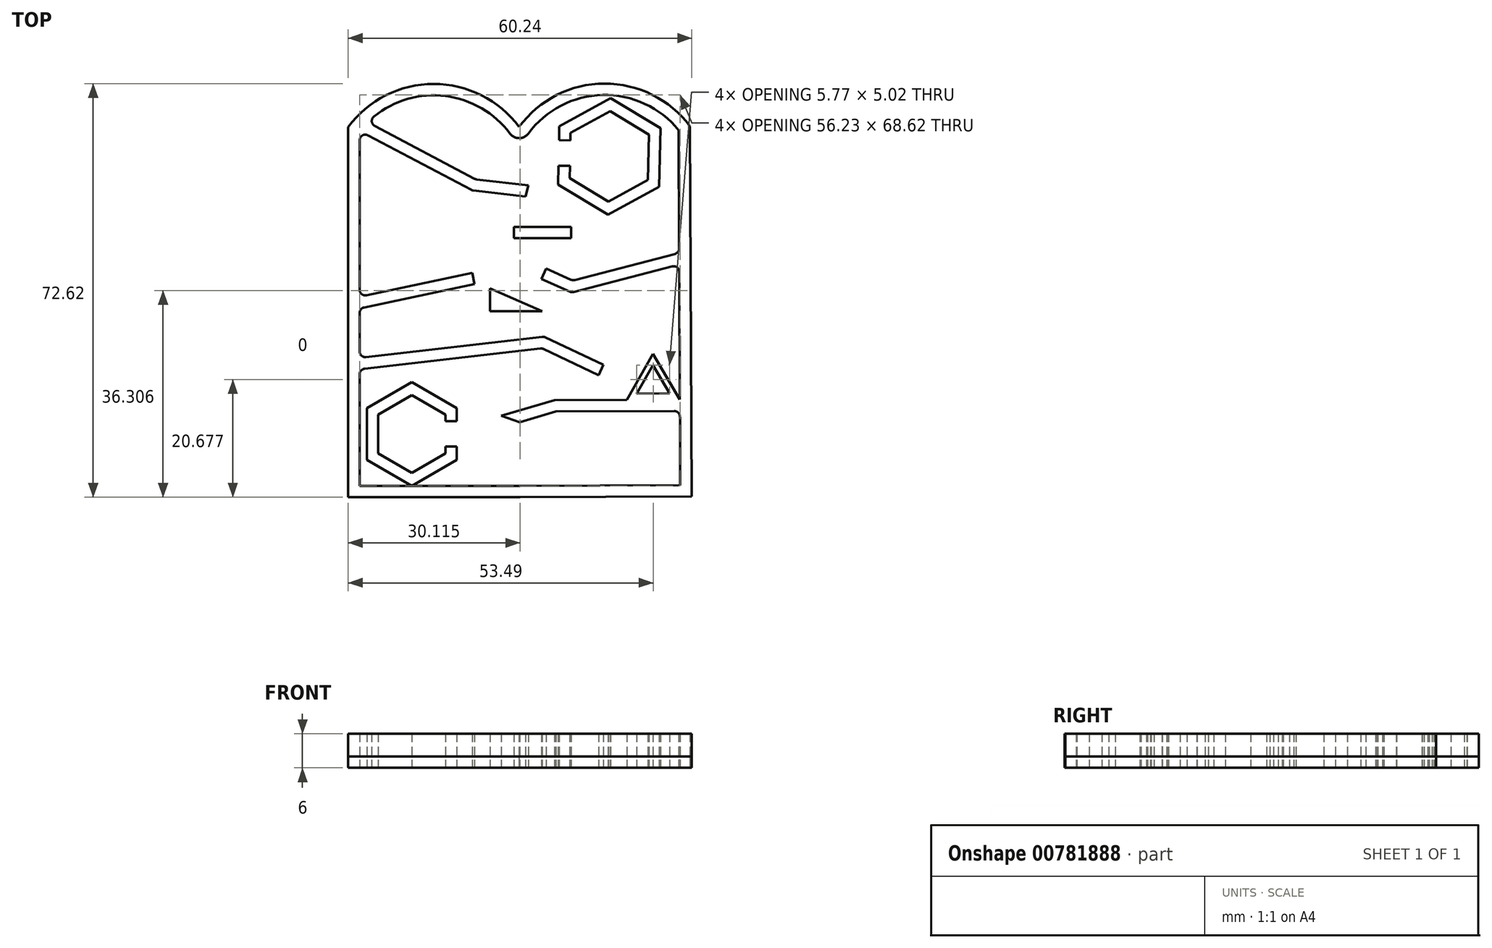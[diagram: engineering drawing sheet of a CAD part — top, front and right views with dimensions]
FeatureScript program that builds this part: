
annotation { "Feature Type Name" : "Feature", "Feature Type Description" : "" }
export const myFeature = defineFeature(function(context is Context, id is Id, definition is map)
    precondition{}
    {
        {
            var Q0;
            Q0=qCreatedBy(makeId("Top.planeOp"),FACE);
            var sketch = newSketch(context, id + "F0", { "sketchPlane" : qUnion([Q0])});
            skCircle(sketch, "E0", {"center": v(0, 0) * mm, "radius": 50 * mm, "construction": true});
            skLineSegment(sketch, "E1.top", {"start": v(-30, -32.65) * mm, "end": v(0.32, -32.65) * mm});
            skLineSegment(sketch, "E1.left", {"start": v(-30, 32.35) * mm, "end": v(-30, -32.65) * mm});
            skArc(sketch, "E2", {"start": v(-0.02, 32.38) * mm, "mid": v(-15.02, 39.9) * mm, "end": v(-30, 32.35) * mm});
            skLineSegment(sketch, "E3", {"start": v(0, 21.27) * mm, "end": v(0, 21.27) * mm});
            skLineSegment(sketch, "E4.0", {"start": v(-28, -30.65) * mm, "end": v(0.11, -30.65) * mm});
            skLineSegment(sketch, "E4.1", {"start": v(-28, 30) * mm, "end": v(-28, 3.79) * mm});
            skArc(sketch, "E4.2", {"start": v(-1.64, 31.2) * mm, "mid": v(-12.94, 37.77) * mm, "end": v(-25.5, 34.18) * mm});
            skArc(sketch, "E5.MirrorCS", {"start": v(-0.02, 32.38) * mm, "mid": v(14.94, 39.97) * mm, "end": v(29.95, 32.48) * mm});
            skArc(sketch, "E6.MirrorCS", {"start": v(1.6, 31.21) * mm, "mid": v(14.64, 37.96) * mm, "end": v(27.95, 31.8) * mm});
            skLineSegment(sketch, "E7.MirrorCS", {"start": v(27.95, 31.8) * mm, "end": v(28.05, 11.04) * mm});
            skLineSegment(sketch, "E8.MirrorCS", {"start": v(29.95, 32.48) * mm, "end": v(30.24, -32.52) * mm});
            skLineSegment(sketch, "E9.MirrorCS", {"start": v(28.23, -30.53) * mm, "end": v(0.11, -30.65) * mm});
            skLineSegment(sketch, "E10.MirrorCS", {"start": v(30.24, -32.52) * mm, "end": v(-0.08, -32.65) * mm});
            skLineSegment(sketch, "E11", {"start": v(-26.53, 30.89) * mm, "end": v(-8.45, 21.32) * mm});
            skLineSegment(sketch, "E12", {"start": v(-8.1, 21.21) * mm, "end": v(1.11, 20.14) * mm});
            skLineSegment(sketch, "E13", {"start": v(26.81, 7.87) * mm, "end": v(9.54, 3.39) * mm});
            skLineSegment(sketch, "E14", {"start": v(8.88, 3.44) * mm, "end": v(3.9, 5.68) * mm});
            skLineSegment(sketch, "E15", {"start": v(-27.2, 0.68) * mm, "end": v(-7.88, 4.78) * mm});
            skLineSegment(sketch, "E16", {"start": v(-27.11, -10.08) * mm, "end": v(3.67, -6.53) * mm});
            skLineSegment(sketch, "E17", {"start": v(4.21, -6.62) * mm, "end": v(13.89, -11.2) * mm});
            skLineSegment(sketch, "E18", {"start": v(27.17, -17.5) * mm, "end": v(6.43, -17.6) * mm});
            skLineSegment(sketch, "E19", {"start": v(6.43, -17.6) * mm, "end": v(0.1, -19.46) * mm});
            skLineSegment(sketch, "E20.0", {"start": v(-7.5, 23.16) * mm, "end": v(1.59, 22.1) * mm});
            skLineSegment(sketch, "E20.1", {"start": v(-25.34, 32.52) * mm, "end": v(-7.84, 23.26) * mm});
            skLineSegment(sketch, "E21", {"start": v(1.59, 22.1) * mm, "end": v(1.11, 20.14) * mm});
            skLineSegment(sketch, "E22.0", {"start": v(9.06, 5.56) * mm, "end": v(4.72, 7.5) * mm});
            skLineSegment(sketch, "E22.1", {"start": v(27.3, 10.07) * mm, "end": v(9.72, 5.5) * mm});
            skLineSegment(sketch, "E23", {"start": v(4.72, 7.5) * mm, "end": v(3.9, 5.68) * mm});
            skLineSegment(sketch, "E24.0", {"start": v(-26.8, 2.8) * mm, "end": v(-8.23, 6.75) * mm});
            skLineSegment(sketch, "E25.0", {"start": v(4.55, -4.57) * mm, "end": v(14.74, -9.4) * mm});
            skLineSegment(sketch, "E25.1", {"start": v(-26.89, -8.04) * mm, "end": v(4, -4.48) * mm});
            skLineSegment(sketch, "E26", {"start": v(14.74, -9.4) * mm, "end": v(13.89, -11.2) * mm});
            skLineSegment(sketch, "E27.0", {"start": v(6.14, -15.6) * mm, "end": v(-3.14, -18.32) * mm});
            skLineSegment(sketch, "E28", {"start": v(0.1, -19.46) * mm, "end": v(-3.14, -18.32) * mm});
            skLineSegment(sketch, "E29", {"start": v(-8.23, 6.75) * mm, "end": v(-7.88, 4.78) * mm});
            skCircle(sketch, "E30.cCircle", {"center": v(15.78, 27.19) * mm, "radius": 7.93 * mm, "construction": true});
            skLineSegment(sketch, "E30.0", {"start": v(22.56, 23.08) * mm, "end": v(15.62, 19.26) * mm});
            skLineSegment(sketch, "E30.1", {"start": v(15.62, 19.26) * mm, "end": v(8.83, 23.36) * mm});
            skLineSegment(sketch, "E30.2", {"start": v(8.83, 23.36) * mm, "end": v(8.88, 25.5) * mm});
            skLineSegment(sketch, "E30.3", {"start": v(9, 31.3) * mm, "end": v(15.94, 35.11) * mm});
            skLineSegment(sketch, "E30.4", {"start": v(15.94, 35.11) * mm, "end": v(22.73, 31) * mm});
            skLineSegment(sketch, "E30.5", {"start": v(22.73, 31) * mm, "end": v(22.56, 23.08) * mm});
            skLineSegment(sketch, "E31", {"start": v(8.97, 30) * mm, "end": v(9, 31.3) * mm});
            skLineSegment(sketch, "E32.0", {"start": v(6.8, 22.25) * mm, "end": v(6.88, 25.55) * mm});
            skLineSegment(sketch, "E32.1", {"start": v(15.57, 16.95) * mm, "end": v(6.8, 22.25) * mm});
            skLineSegment(sketch, "E32.2", {"start": v(24.54, 21.88) * mm, "end": v(15.57, 16.95) * mm});
            skLineSegment(sketch, "E32.3", {"start": v(6.97, 30.05) * mm, "end": v(7.02, 32.49) * mm});
            skLineSegment(sketch, "E32.4", {"start": v(7.02, 32.49) * mm, "end": v(16, 37.42) * mm});
            skLineSegment(sketch, "E32.5", {"start": v(16, 37.42) * mm, "end": v(24.75, 32.12) * mm});
            skLineSegment(sketch, "E32.6", {"start": v(24.75, 32.12) * mm, "end": v(24.54, 21.88) * mm});
            skLineSegment(sketch, "E33", {"start": v(6.88, 25.55) * mm, "end": v(8.88, 25.5) * mm});
            skLineSegment(sketch, "E34", {"start": v(8.97, 30) * mm, "end": v(6.97, 30.05) * mm});
            skLineSegment(sketch, "E35", {"start": v(28.06, 6.91) * mm, "end": v(28.16, -15.5) * mm});
            skLineSegment(sketch, "E36", {"start": v(-28, 31.67) * mm, "end": v(-28, 31.67) * mm});
            skLineSegment(sketch, "E37", {"start": v(-28, -0.3) * mm, "end": v(-28, -7.04) * mm});
            skLineSegment(sketch, "E38", {"start": v(-28, -11.07) * mm, "end": v(-28, -30.65) * mm});
            skLineSegment(sketch, "E39", {"start": v(28.18, -18.5) * mm, "end": v(28.23, -30.53) * mm});
            skLineSegment(sketch, "E40", {"start": v(-0.93, 14.82) * mm, "end": v(-0.93, 12.82) * mm});
            skLineSegment(sketch, "E41", {"start": v(-0.93, 12.82) * mm, "end": v(9.07, 12.82) * mm});
            skLineSegment(sketch, "E42", {"start": v(9.07, 12.82) * mm, "end": v(9.07, 14.82) * mm});
            skLineSegment(sketch, "E43", {"start": v(9.07, 14.82) * mm, "end": v(-0.93, 14.82) * mm});
            skCircle(sketch, "E44.cCircle", {"center": v(23.48, -12.8) * mm, "radius": 3.33 * mm, "construction": true});
            skLineSegment(sketch, "E44.0", {"start": v(23.45, -9.46) * mm, "end": v(26.37, -14.43) * mm});
            skLineSegment(sketch, "E44.1", {"start": v(26.37, -14.43) * mm, "end": v(20.6, -14.48) * mm});
            skLineSegment(sketch, "E44.2", {"start": v(20.6, -14.48) * mm, "end": v(23.45, -9.46) * mm});
            skCircle(sketch, "E45.cCircle", {"center": v(-18.86, -21.54) * mm, "radius": 6.8 * mm, "construction": true});
            skLineSegment(sketch, "E45.0", {"start": v(-18.86, -14.74) * mm, "end": v(-12.97, -18.14) * mm});
            skLineSegment(sketch, "E45.1", {"start": v(-12.97, -18.14) * mm, "end": v(-12.97, -19.27) * mm});
            skLineSegment(sketch, "E45.2", {"start": v(-12.97, -24.94) * mm, "end": v(-18.86, -28.34) * mm});
            skLineSegment(sketch, "E45.3", {"start": v(-18.86, -28.34) * mm, "end": v(-24.75, -24.94) * mm});
            skLineSegment(sketch, "E45.4", {"start": v(-24.75, -24.94) * mm, "end": v(-24.75, -18.14) * mm});
            skLineSegment(sketch, "E45.5", {"start": v(-24.75, -18.14) * mm, "end": v(-18.86, -14.74) * mm});
            skLineSegment(sketch, "E46.2", {"start": v(23.43, -7.46) * mm, "end": v(28.16, -15.5) * mm});
            skLineSegment(sketch, "E47", {"start": v(18.85, -15.55) * mm, "end": v(18.85, -15.55) * mm});
            skLineSegment(sketch, "E48", {"start": v(28.16, -15.5) * mm, "end": v(28.16, -15.5) * mm});
            skLineSegment(sketch, "E49", {"start": v(18.85, -15.55) * mm, "end": v(23.43, -7.46) * mm});
            skLineSegment(sketch, "E50", {"start": v(18.85, -15.55) * mm, "end": v(6.14, -15.6) * mm});
            skLineSegment(sketch, "E51", {"start": v(-12.97, -23.77) * mm, "end": v(-12.97, -24.94) * mm});
            skLineSegment(sketch, "E52.0", {"start": v(-10.97, -16.99) * mm, "end": v(-10.97, -19.27) * mm});
            skLineSegment(sketch, "E52.1", {"start": v(-18.86, -12.44) * mm, "end": v(-10.97, -16.99) * mm});
            skLineSegment(sketch, "E52.2", {"start": v(-26.75, -16.99) * mm, "end": v(-18.86, -12.44) * mm});
            skLineSegment(sketch, "E52.3", {"start": v(-10.97, -23.77) * mm, "end": v(-10.97, -26.1) * mm});
            skLineSegment(sketch, "E52.4", {"start": v(-10.97, -26.1) * mm, "end": v(-18.86, -30.65) * mm});
            skLineSegment(sketch, "E52.5", {"start": v(-18.86, -30.65) * mm, "end": v(-26.75, -26.1) * mm});
            skLineSegment(sketch, "E52.6", {"start": v(-26.75, -26.1) * mm, "end": v(-26.75, -16.99) * mm});
            skLineSegment(sketch, "E53", {"start": v(-12.97, -23.77) * mm, "end": v(-10.97, -23.77) * mm});
            skLineSegment(sketch, "E54", {"start": v(-12.97, -19.27) * mm, "end": v(-10.97, -19.27) * mm});
            skLineSegment(sketch, "E55", {"start": v(-5.14, 0) * mm, "end": v(-5.14, 4) * mm});
            skLineSegment(sketch, "E56", {"start": v(-5.14, 4) * mm, "end": v(4.03, 0) * mm});
            skLineSegment(sketch, "E57", {"start": v(4.03, 0) * mm, "end": v(-5.14, 0) * mm});
            skPoint(sketch, "E58.visualSharp", {"position": v(-26.61, 33.2) * mm});
            skArc(sketch, "E58.filletArc", {"start": v(-25.5, 34.18) * mm, "mid": v(-25.86, 33.3) * mm, "end": v(-25.34, 32.52) * mm});
            skPoint(sketch, "E59.orphan", {"position": v(-0.05, 32.35) * mm});
            skPoint(sketch, "E60.start.orphan", {"position": v(0, 32.35) * mm});
            skArc(sketch, "E61", {"start": v(-1.64, 31.2) * mm, "mid": v(-0.02, 30.4) * mm, "end": v(1.6, 31.21) * mm});
            skPoint(sketch, "E62.visualSharp", {"position": v(-28, 31.67) * mm});
            skArc(sketch, "E62.filletArc", {"start": v(-26.53, 30.89) * mm, "mid": v(-27.52, 30.86) * mm, "end": v(-28, 30) * mm});
            skPoint(sketch, "E63.visualSharp", {"position": v(28.05, 10.26) * mm});
            skArc(sketch, "E63.filletArc", {"start": v(27.3, 10.07) * mm, "mid": v(27.84, 10.42) * mm, "end": v(28.05, 11.04) * mm});
            skPoint(sketch, "E64.visualSharp", {"position": v(28.06, 8.2) * mm});
            skArc(sketch, "E64.filletArc", {"start": v(28.06, 6.91) * mm, "mid": v(27.67, 7.7) * mm, "end": v(26.81, 7.87) * mm});
            skPoint(sketch, "E65.visualSharp", {"position": v(-28, 2.55) * mm});
            skArc(sketch, "E65.filletArc", {"start": v(-28, 3.79) * mm, "mid": v(-27.63, 3) * mm, "end": v(-26.8, 2.8) * mm});
            skPoint(sketch, "E66.visualSharp", {"position": v(-28, 0.5) * mm});
            skArc(sketch, "E66.filletArc", {"start": v(-27.2, 0.68) * mm, "mid": v(-27.78, 0.33) * mm, "end": v(-28, -0.3) * mm});
            skPoint(sketch, "E67.visualSharp", {"position": v(28.17, -17.5) * mm});
            skArc(sketch, "E67.filletArc", {"start": v(28.18, -18.5) * mm, "mid": v(27.88, -17.8) * mm, "end": v(27.17, -17.5) * mm});
            skPoint(sketch, "E68.visualSharp", {"position": v(-28, -8.17) * mm});
            skArc(sketch, "E68.filletArc", {"start": v(-28, -7.04) * mm, "mid": v(-27.67, -7.8) * mm, "end": v(-26.89, -8.04) * mm});
            skPoint(sketch, "E69.visualSharp", {"position": v(-28, -10.18) * mm});
            skArc(sketch, "E69.filletArc", {"start": v(-27.11, -10.08) * mm, "mid": v(-27.75, -10.4) * mm, "end": v(-28, -11.07) * mm});
            skPoint(sketch, "E70.visualSharp", {"position": v(4.3, -4.44) * mm});
            skArc(sketch, "E70.filletArc", {"start": v(4.55, -4.57) * mm, "mid": v(4.29, -4.48) * mm, "end": v(4, -4.48) * mm});
            skPoint(sketch, "E71.visualSharp", {"position": v(3.95, -6.5) * mm});
            skArc(sketch, "E71.filletArc", {"start": v(4.21, -6.62) * mm, "mid": v(3.95, -6.54) * mm, "end": v(3.67, -6.53) * mm});
            skPoint(sketch, "E72.visualSharp", {"position": v(9.38, 5.41) * mm});
            skArc(sketch, "E72.filletArc", {"start": v(9.06, 5.56) * mm, "mid": v(9.38, 5.47) * mm, "end": v(9.72, 5.5) * mm});
            skPoint(sketch, "E73.visualSharp", {"position": v(9.2, 3.3) * mm});
            skArc(sketch, "E73.filletArc", {"start": v(8.88, 3.44) * mm, "mid": v(9.2, 3.36) * mm, "end": v(9.54, 3.39) * mm});
            skPoint(sketch, "E74.visualSharp", {"position": v(-7.68, 23.18) * mm});
            skArc(sketch, "E74.filletArc", {"start": v(-7.84, 23.26) * mm, "mid": v(-7.67, 23.2) * mm, "end": v(-7.5, 23.16) * mm});
            skPoint(sketch, "E75.visualSharp", {"position": v(-8.28, 21.23) * mm});
            skArc(sketch, "E75.filletArc", {"start": v(-8.45, 21.32) * mm, "mid": v(-8.28, 21.25) * mm, "end": v(-8.1, 21.21) * mm});
            skLineSegment(sketch, "E76", {"start": v(6.97, 30.05) * mm, "end": v(6.88, 25.55) * mm});
            skSolve(sketch);
        }
        {
            var Q0;
            Q0 = qSketchRegion(id + "F0", true);
            var Q1;
            Q1=makeQuery(id+"F0.imprint","IMPRINT",FACE,{"disambiguationData":[TD([[makeQuery(id+"F0.imprint","IMPRINT",EDGE,{"derivedFrom":sQuery(id+"F0.wireOp",EDGE,"E30.0")}),1.0]])]});
            var Q2;
            Q2=makeQuery(id+"F0.imprint","IMPRINT",FACE,{"disambiguationData":[TD([[makeQuery(id+"F0.imprint","IMPRINT",EDGE,{"derivedFrom":sQuery(id+"F0.wireOp",EDGE,"E40")}),1.0]])]});
            var Q3;
            Q3=makeQuery(id+"F0.imprint","IMPRINT",FACE,{"disambiguationData":[TD([[makeQuery(id+"F0.imprint","IMPRINT",EDGE,{"derivedFrom":sQuery(id+"F0.wireOp",EDGE,"E55")}),-1.0]])]});
            var Q4;
            Q4=makeQuery(id+"F0.imprint","IMPRINT",FACE,{"disambiguationData":[TD([[makeQuery(id+"F0.imprint","IMPRINT",EDGE,{"derivedFrom":sQuery(id+"F0.wireOp",EDGE,"E45.0")}),1.0]])]});
            extrude(context, id + "F1", {"entities" : qUnion([Q0, Q1, Q2, Q3, Q4]), "depth" : 6 * mm, "offsetDistance" : 25 * mm});
        }
        {
            var Q0;
            Q0=qCreatedBy(makeId("Top.planeOp"),FACE);
            var sketch = newSketch(context, id + "F2", { "sketchPlane" : qUnion([Q0])});
            skLineSegment(sketch, "E77.0", {"start": v(-30, -32.65) * mm, "end": v(0.12, -32.65) * mm});
            skLineSegment(sketch, "E78.0", {"start": v(30.24, -32.52) * mm, "end": v(0.12, -32.65) * mm});
            skLineSegment(sketch, "E79.0", {"start": v(29.95, 32.48) * mm, "end": v(30.24, -32.52) * mm});
            skArc(sketch, "E80.0", {"start": v(-0.02, 32.38) * mm, "mid": v(14.94, 39.97) * mm, "end": v(29.95, 32.48) * mm});
            skArc(sketch, "E81.0", {"start": v(-0.02, 32.38) * mm, "mid": v(-15.02, 39.9) * mm, "end": v(-30, 32.35) * mm});
            skLineSegment(sketch, "E82.0", {"start": v(-30, 32.35) * mm, "end": v(-30, -32.65) * mm});
            skSolve(sketch);
        }
        {
            var Q0;
            Q0 = qSketchRegion(id + "F2", true);
            extrude(context, id + "F3", {"entities" : qUnion([Q0]), "depth" : 2 * mm, "offsetDistance" : 25 * mm});
        }
    });
